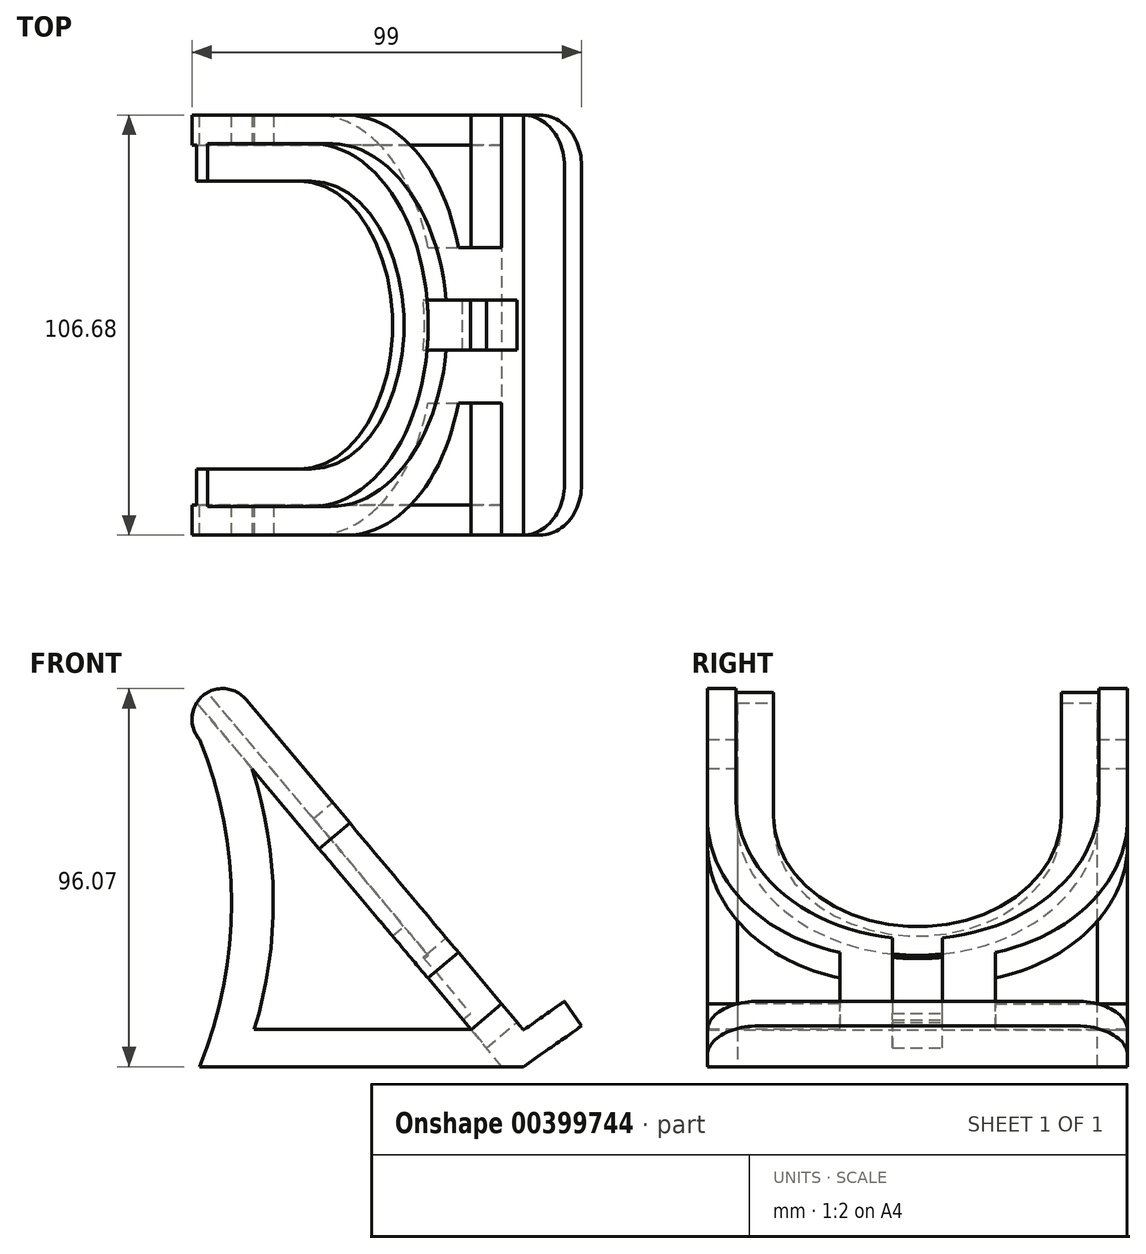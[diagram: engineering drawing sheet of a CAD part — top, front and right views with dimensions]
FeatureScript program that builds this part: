
annotation { "Feature Type Name" : "Feature", "Feature Type Description" : "" }
export const myFeature = defineFeature(function(context is Context, id is Id, definition is map)
    precondition{}
    {
        {
            var Q0;
            Q0=qCreatedBy(makeId("Front.planeOp"),FACE);
            var sketch = newSketch(context, id + "F0", { "sketchPlane" : qUnion([Q0])});
            skLineSegment(sketch, "E0", {"start": v(-26.46, -52) * mm, "end": v(55.88, -52) * mm});
            skLineSegment(sketch, "E1", {"start": v(55.88, -52) * mm, "end": v(70.65, -41.63) * mm});
            skLineSegment(sketch, "E2", {"start": v(70.65, -41.63) * mm, "end": v(66.27, -35.4) * mm});
            skLineSegment(sketch, "E3", {"start": v(66.27, -35.4) * mm, "end": v(55.88, -42.68) * mm});
            skLineSegment(sketch, "E4", {"start": v(55.88, -42.68) * mm, "end": v(-14.6, 41.3) * mm});
            skArc(sketch, "E5", {"start": v(-26.46, -52) * mm, "mid": v(-18.29, -10.4) * mm, "end": v(-26.46, 31.2) * mm});
            skArc(sketch, "E6", {"start": v(-14.6, 41.3) * mm, "mid": v(-25.6, 42.22) * mm, "end": v(-26.46, 31.2) * mm});
            skSolve(sketch);
        }
        {
            var Q0;
            Q0=makeQuery(id+"F0.imprint","IMPRINT",FACE,{"disambiguationData":[TD([[makeQuery(id+"F0.imprint","IMPRINT",EDGE,{"derivedFrom":sQuery(id+"F0.wireOp",EDGE,"E0")}),1.0]])]});
            var Q1;
            Q1 = qSketchRegion(id + "F2", true);
            extrude(context, id + "F1", {"entities" : qUnion([Q0, Q1]), "endBound" : BoundingType.SYMMETRIC, "depth" : 106.68 * mm});
        }
        {
            var Q0;
            Q0=makeQuery(id+"F1.opExtrude","SWEPT_FACE",FACE,{"disambiguationData":[OSD([sQuery(id+"F0.wireOp",EDGE,"E4")])]});
            var sketch = newSketch(context, id + "F2", { "sketchPlane" : qUnion([Q0])});
            skCircle(sketch, "E7", {"center": v(0, 7.58) * mm, "radius": 46.1 * mm});
            skLineSegment(sketch, "E8", {"start": v(0, 7.58) * mm, "end": v(-46.1, 7.58) * mm, "construction": true});
            skLineSegment(sketch, "E9", {"start": v(-46.1, 7.58) * mm, "end": v(-46.1, 73.2) * mm});
            skLineSegment(sketch, "E10", {"start": v(-46.1, 73.2) * mm, "end": v(0, 73.2) * mm});
            skLineSegment(sketch, "E11", {"start": v(0, 73.2) * mm, "end": v(0, 7.58) * mm});
            skLineSegment(sketch, "E12", {"start": v(-46.1, 7.58) * mm, "end": v(0, 7.58) * mm});
            skLineSegment(sketch, "E13.MirrorCS", {"start": v(0, 1.39) * mm, "end": v(46.1, 1.39) * mm, "construction": true});
            skLineSegment(sketch, "E14.MirrorCS", {"start": v(46.1, -1.53) * mm, "end": v(46.05, 73.08) * mm});
            skLineSegment(sketch, "E15.MirrorCS", {"start": v(46.05, 73.08) * mm, "end": v(0, 73.2) * mm});
            skLineSegment(sketch, "E16", {"start": v(-6.35, -38.08) * mm, "end": v(-6.35, -66.02) * mm});
            skLineSegment(sketch, "E17", {"start": v(-6.35, -66.02) * mm, "end": v(6.35, -66.02) * mm});
            skLineSegment(sketch, "E18", {"start": v(6.35, -66.02) * mm, "end": v(6.35, -38.08) * mm});
            skCircle(sketch, "E19", {"center": v(0, 7.58) * mm, "radius": 36.56 * mm});
            skLineSegment(sketch, "E20", {"start": v(-36.56, 7.58) * mm, "end": v(-36.56, 73.2) * mm});
            skLineSegment(sketch, "E21.MirrorCS", {"start": v(36.56, 7.58) * mm, "end": v(36.56, 73.2) * mm});
            skLineSegment(sketch, "E22", {"start": v(-6.35, -56.67) * mm, "end": v(6.35, -56.67) * mm});
            skArc(sketch, "E23", {"start": v(-53.34, 0) * mm, "mid": v(-42.57, -28.16) * mm, "end": v(-16.69, -43.64) * mm});
            skLineSegment(sketch, "E24", {"start": v(-19.75, -42.9) * mm, "end": v(-19.75, -59.96) * mm});
            skLineSegment(sketch, "E25", {"start": v(-19.75, -59.96) * mm, "end": v(-53.34, -59.96) * mm});
            skLineSegment(sketch, "E26", {"start": v(-53.34, -59.96) * mm, "end": v(-53.34, 0) * mm});
            skArc(sketch, "E27.MirrorCS", {"start": v(53.34, 0) * mm, "mid": v(42.57, -28.16) * mm, "end": v(16.69, -43.64) * mm});
            skLineSegment(sketch, "E28.MirrorCS", {"start": v(19.75, -42.9) * mm, "end": v(19.75, -59.96) * mm});
            skLineSegment(sketch, "E29.MirrorCS", {"start": v(19.75, -59.96) * mm, "end": v(53.34, -59.96) * mm});
            skLineSegment(sketch, "E30.MirrorCS", {"start": v(53.34, -59.96) * mm, "end": v(53.34, 0) * mm});
            skSolve(sketch);
        }
        {
            var Q0;
            {var subQ1=sQuery(id+"F2.wireOp",EDGE,"E7");var subQ3=sQuery(id+"F2.wireOp",EDGE,"E20");var subQ4=makeQuery(id+"F2.imprint","INTERSECT",VERTEX,{"derivedFrom":[subQ1,subQ3]});Q0=makeQuery(id+"F2.imprint","IMPRINT",FACE,{"disambiguationData":[TD([[makeQuery(id+"F2.imprint","IMPRINT",EDGE,{"disambiguationData":[TD([[subQ4,-1.0]])],"derivedFrom":subQ1}),1.0]])]});}
            var Q1;
            {var subQ0=sQuery(id+"F2.wireOp",EDGE,"E21.MirrorCS");var subQ1=sQuery(id+"F2.wireOp",EDGE,"E7");var subQ2=makeQuery(id+"F2.imprint","INTERSECT",VERTEX,{"derivedFrom":[subQ1,subQ0]});Q1=makeQuery(id+"F2.imprint","IMPRINT",FACE,{"disambiguationData":[TD([[makeQuery(id+"F2.imprint","IMPRINT",EDGE,{"disambiguationData":[TD([[subQ2,1.0]])],"derivedFrom":subQ1}),-1.0]])]});}
            var Q2;
            {var subQ0=sQuery(id+"F2.wireOp",EDGE,"E11");var subQ3=sQuery(id+"F2.wireOp",EDGE,"E7");var subQ4=makeQuery(id+"F2.imprint","INTERSECT",VERTEX,{"derivedFrom":[subQ3,subQ0]});Q2=makeQuery(id+"F2.imprint","IMPRINT",FACE,{"disambiguationData":[TD([[makeQuery(id+"F2.imprint","IMPRINT",EDGE,{"disambiguationData":[TD([[subQ4,-1.0]])],"derivedFrom":subQ3}),-1.0]])]});}
            var Q3;
            {var subQ0=sQuery(id+"F2.wireOp",EDGE,"E10");var subQ1=sQuery(id+"F2.wireOp",EDGE,"E9");var subQ2=makeQuery(id+"F2.imprint","INTERSECT",VERTEX,{"derivedFrom":[subQ1,subQ0]});Q3=makeQuery(id+"F2.imprint","IMPRINT",FACE,{"disambiguationData":[TD([[makeQuery(id+"F2.imprint","IMPRINT",EDGE,{"disambiguationData":[TD([[subQ2,-1.0]])],"derivedFrom":subQ0}),-1.0]])]});}
            var Q4;
            {var subQ0=sQuery(id+"F2.wireOp",EDGE,"E15.MirrorCS");var subQ1=sQuery(id+"F2.wireOp",EDGE,"E14.MirrorCS");var subQ2=makeQuery(id+"F2.imprint","INTERSECT",VERTEX,{"derivedFrom":[subQ1,subQ0]});Q4=makeQuery(id+"F2.imprint","IMPRINT",FACE,{"disambiguationData":[TD([[makeQuery(id+"F2.imprint","IMPRINT",EDGE,{"disambiguationData":[TD([[subQ2,-1.0]])],"derivedFrom":subQ0}),1.0]])]});}
            var Q5;
            {var subQ0=sQuery(id+"F2.wireOp",EDGE,"E11");var subQ1=sQuery(id+"F2.wireOp",EDGE,"E7");var subQ2=makeQuery(id+"F2.imprint","INTERSECT",VERTEX,{"derivedFrom":[subQ1,subQ0]});Q5=makeQuery(id+"F2.imprint","IMPRINT",FACE,{"disambiguationData":[TD([[makeQuery(id+"F2.imprint","IMPRINT",EDGE,{"disambiguationData":[TD([[subQ2,-1.0]])],"derivedFrom":subQ1}),1.0]])]});}
            var Q6;
            {var subQ0=sQuery(id+"F2.wireOp",EDGE,"E11");var subQ1=sQuery(id+"F2.wireOp",EDGE,"E7");var subQ2=makeQuery(id+"F2.imprint","INTERSECT",VERTEX,{"derivedFrom":[subQ1,subQ0]});Q6=makeQuery(id+"F2.imprint","IMPRINT",FACE,{"disambiguationData":[TD([[makeQuery(id+"F2.imprint","IMPRINT",EDGE,{"disambiguationData":[TD([[subQ2,1.0]])],"derivedFrom":subQ1}),1.0]])]});}
            var Q7;
            {var subQ1=sQuery(id+"F2.wireOp",EDGE,"E7");var subQ3=sQuery(id+"F2.wireOp",EDGE,"E20");var subQ4=makeQuery(id+"F2.imprint","INTERSECT",VERTEX,{"derivedFrom":[subQ1,subQ3]});Q7=makeQuery(id+"F2.imprint","IMPRINT",FACE,{"disambiguationData":[TD([[makeQuery(id+"F2.imprint","IMPRINT",EDGE,{"disambiguationData":[TD([[subQ4,-1.0]])],"derivedFrom":subQ1}),-1.0]])]});}
            var Q8;
            {var subQ5=sQuery(id+"F2.wireOp",EDGE,"E11");var subQ7=sQuery(id+"F2.wireOp",EDGE,"E7");var subQ8=makeQuery(id+"F2.imprint","INTERSECT",VERTEX,{"derivedFrom":[subQ7,subQ5]});Q8=makeQuery(id+"F2.imprint","IMPRINT",FACE,{"disambiguationData":[TD([[makeQuery(id+"F2.imprint","IMPRINT",EDGE,{"disambiguationData":[TD([[subQ8,1.0]])],"derivedFrom":subQ7}),-1.0]])]});}
            var Q9;
            {var subQ0=sQuery(id+"F2.wireOp",EDGE,"E20");var subQ1=sQuery(id+"F2.wireOp",EDGE,"E7");var subQ2=makeQuery(id+"F2.imprint","INTERSECT",VERTEX,{"derivedFrom":[subQ1,subQ0]});Q9=makeQuery(id+"F2.imprint","IMPRINT",FACE,{"disambiguationData":[TD([[makeQuery(id+"F2.imprint","IMPRINT",EDGE,{"disambiguationData":[TD([[subQ2,1.0]])],"derivedFrom":subQ1}),-1.0]])]});}
            var Q10;
            {var subQ0=sQuery(id+"F2.wireOp",EDGE,"E20");var subQ3=sQuery(id+"F2.wireOp",EDGE,"E7");var subQ4=makeQuery(id+"F2.imprint","INTERSECT",VERTEX,{"derivedFrom":[subQ3,subQ0]});Q10=makeQuery(id+"F2.imprint","IMPRINT",FACE,{"disambiguationData":[TD([[makeQuery(id+"F2.imprint","IMPRINT",EDGE,{"disambiguationData":[TD([[subQ4,1.0]])],"derivedFrom":subQ3}),1.0]])]});}
            var Q11;
            {var subQ0=sQuery(id+"F2.wireOp",EDGE,"E21.MirrorCS");var subQ1=sQuery(id+"F2.wireOp",EDGE,"E19");var subQ2=makeQuery(id+"F2.imprint","INTERSECT",VERTEX,{"derivedFrom":[subQ1,subQ0]});Q11=makeQuery(id+"F2.imprint","IMPRINT",FACE,{"disambiguationData":[TD([[makeQuery(id+"F2.imprint","IMPRINT",EDGE,{"disambiguationData":[TD([[subQ2,-1.0]])],"derivedFrom":subQ1}),-1.0]])]});}
            var Q12;
            {var subQ0=sQuery(id+"F2.wireOp",EDGE,"E7");var subQ7=sQuery(id+"F2.wireOp",EDGE,"E21.MirrorCS");var subQ11=makeQuery(id+"F2.imprint","INTERSECT",VERTEX,{"derivedFrom":[subQ0,subQ7]});Q12=makeQuery(id+"F2.imprint","IMPRINT",FACE,{"disambiguationData":[TD([[makeQuery(id+"F2.imprint","IMPRINT",EDGE,{"disambiguationData":[TD([[subQ11,1.0]])],"derivedFrom":subQ0}),1.0]])]});}
            var Q13;
            {var subQ0=sQuery(id+"F2.wireOp",EDGE,"E12");var subQ1=sQuery(id+"F2.wireOp",EDGE,"E11");var subQ2=makeQuery(id+"F2.imprint","INTERSECT",VERTEX,{"derivedFrom":[subQ1,subQ0]});Q13=makeQuery(id+"F2.imprint","IMPRINT",FACE,{"disambiguationData":[TD([[makeQuery(id+"F2.imprint","IMPRINT",EDGE,{"disambiguationData":[TD([[subQ2,1.0]])],"derivedFrom":subQ1}),1.0]])]});}
            var Q14;
            {var subQ0=sQuery(id+"F2.wireOp",EDGE,"E12");var subQ1=sQuery(id+"F2.wireOp",EDGE,"E11");var subQ2=makeQuery(id+"F2.imprint","INTERSECT",VERTEX,{"derivedFrom":[subQ1,subQ0]});Q14=makeQuery(id+"F2.imprint","IMPRINT",FACE,{"disambiguationData":[TD([[makeQuery(id+"F2.imprint","IMPRINT",EDGE,{"disambiguationData":[TD([[subQ2,1.0]])],"derivedFrom":subQ1}),-1.0]])]});}
            var Q15;
            {var subQ0=sQuery(id+"F2.wireOp",EDGE,"E21.MirrorCS");var subQ1=sQuery(id+"F2.wireOp",EDGE,"E7");var subQ2=makeQuery(id+"F2.imprint","INTERSECT",VERTEX,{"derivedFrom":[subQ1,subQ0]});Q15=makeQuery(id+"F2.imprint","IMPRINT",FACE,{"disambiguationData":[TD([[makeQuery(id+"F2.imprint","IMPRINT",EDGE,{"disambiguationData":[TD([[subQ2,-1.0]])],"derivedFrom":subQ1}),-1.0]])]});}
            extrude(context, id + "F3", {"entities" : qUnion([Q0, Q1, Q2, Q3, Q4, Q5, Q6, Q7, Q8, Q9, Q10, Q11, Q12, Q13, Q14, Q15]), "operationType" : NewBodyOperationType.REMOVE, "oppositeDirection" : true, "depth" : 6.35 * mm});
        }
        {
            var Q0;
            {var subQ0=sQuery(id+"F2.wireOp",EDGE,"E16");Q0=makeQuery(id+"F2.imprint","IMPRINT",FACE,{"disambiguationData":[TD([[makeQuery(id+"F2.imprint","IMPRINT",EDGE,{"derivedFrom":subQ0}),1.0]])]});}
            extrude(context, id + "F4", {"entities" : qUnion([Q0]), "operationType" : NewBodyOperationType.REMOVE, "oppositeDirection" : true, "depth" : 7.62 * mm});
        }
        {
            var Q0;
            Q0=makeQuery(id+"F1.opExtrude","CAP_FACE",FACE,{"disambiguationData":[OSD([sQuery(id+"F0.wireOp",EDGE,"E0"),sQuery(id+"F0.wireOp",EDGE,"E1"),sQuery(id+"F0.wireOp",EDGE,"E2"),sQuery(id+"F0.wireOp",EDGE,"E3"),sQuery(id+"F0.wireOp",EDGE,"E4"),sQuery(id+"F0.wireOp",EDGE,"E5"),sQuery(id+"F0.wireOp",EDGE,"E6")])],"isStart":false});
            var sketch = newSketch(context, id + "F5", { "sketchPlane" : qUnion([Q0])});
            skLineSegment(sketch, "E31", {"start": v(-13.05, 23.66) * mm, "end": v(42.5, -42.55) * mm});
            skArc(sketch, "E32", {"start": v(-12.51, -42.55) * mm, "mid": v(-7.68, -9.4) * mm, "end": v(-13.05, 23.66) * mm});
            skLineSegment(sketch, "E33", {"start": v(-12.51, -42.55) * mm, "end": v(42.5, -42.55) * mm});
            skSolve(sketch);
        }
        {
            var Q0;
            Q0=makeQuery(id+"F5.imprint","IMPRINT",FACE,{"disambiguationData":[TD([[makeQuery(id+"F5.imprint","IMPRINT",EDGE,{"derivedFrom":sQuery(id+"F5.wireOp",EDGE,"E31")}),-1.0]])]});
            var Q1;
            Q1=makeQuery(id+"F5.imprint","IMPRINT",FACE,{"disambiguationData":[TD([[makeQuery(id+"F5.imprint","IMPRINT",EDGE,{"derivedFrom":sQuery(id+"F5.wireOp",EDGE,"wPjwQzWi-Tjyw-v6FZ-FHt0-rqqnCeeGMehr")}),-1.0]])]});
            extrude(context, id + "F6", {"entities" : qUnion([Q0, Q1]), "operationType" : NewBodyOperationType.REMOVE, "endBound" : BoundingType.UP_TO_NEXT, "oppositeDirection" : true, "depth" : 25.4 * mm});
        }
        {
            var Q0;
            Q0=makeQuery(id+"F1.opExtrude","SWEPT_EDGE",EDGE,{"disambiguationData":[OSD([sQuery(id+"F0.wireOp",EDGE,"E0"),sQuery(id+"F0.wireOp",EDGE,"E5")])]});
            cPlane(context, id + "F7", {"entities" : qUnion([Q0]), "cplaneType" : CPlaneType.LINE_ANGLE, "offset" : 40.4 * mm, "angle" : 50 * degree, "width" : 152.4 * mm, "height" : 152.4 * mm});
        }
        {
            var Q0;
            Q0=qCreatedBy(id+"F7.planeOp",FACE);
            var sketch = newSketch(context, id + "F8", { "sketchPlane" : qUnion([Q0])});
            skLineSegment(sketch, "E34", {"start": v(45.72, 83.56) * mm, "end": v(-45.72, 83.56) * mm});
            skLineSegment(sketch, "E35", {"start": v(-45.72, 83.56) * mm, "end": v(-45.72, -100.06) * mm});
            skLineSegment(sketch, "E36", {"start": v(-45.72, -100.06) * mm, "end": v(45.72, -100.06) * mm});
            skLineSegment(sketch, "E37", {"start": v(45.72, -100.06) * mm, "end": v(45.72, 83.56) * mm});
            skSolve(sketch);
        }
        {
            var Q0;
            Q0=makeQuery(id+"F8.imprint","IMPRINT",FACE,{"disambiguationData":[TD([[makeQuery(id+"F8.imprint","IMPRINT",EDGE,{"derivedFrom":sQuery(id+"F8.wireOp",EDGE,"E34")}),1.0]])]});
            extrude(context, id + "F9", {"entities" : qUnion([Q0]), "operationType" : NewBodyOperationType.REMOVE, "depth" : 58.93 * mm});
        }
        {
            var Q0;
            {var subQ0=sQuery(id+"F2.wireOp",EDGE,"E12");var subQ1=sQuery(id+"F2.wireOp",EDGE,"E11");var subQ2=makeQuery(id+"F2.imprint","INTERSECT",VERTEX,{"derivedFrom":[subQ1,subQ0]});Q0=makeQuery(id+"F2.imprint","IMPRINT",FACE,{"disambiguationData":[TD([[makeQuery(id+"F2.imprint","IMPRINT",EDGE,{"disambiguationData":[TD([[subQ2,1.0]])],"derivedFrom":subQ1}),-1.0]])]});}
            var Q1;
            {var subQ0=sQuery(id+"F2.wireOp",EDGE,"E12");var subQ1=sQuery(id+"F2.wireOp",EDGE,"E11");var subQ2=makeQuery(id+"F2.imprint","INTERSECT",VERTEX,{"derivedFrom":[subQ1,subQ0]});Q1=makeQuery(id+"F2.imprint","IMPRINT",FACE,{"disambiguationData":[TD([[makeQuery(id+"F2.imprint","IMPRINT",EDGE,{"disambiguationData":[TD([[subQ2,1.0]])],"derivedFrom":subQ1}),1.0]])]});}
            var Q2;
            {var subQ0=sQuery(id+"F2.wireOp",EDGE,"E20");var subQ3=sQuery(id+"F2.wireOp",EDGE,"E7");var subQ4=makeQuery(id+"F2.imprint","INTERSECT",VERTEX,{"derivedFrom":[subQ3,subQ0]});Q2=makeQuery(id+"F2.imprint","IMPRINT",FACE,{"disambiguationData":[TD([[makeQuery(id+"F2.imprint","IMPRINT",EDGE,{"disambiguationData":[TD([[subQ4,1.0]])],"derivedFrom":subQ3}),1.0]])]});}
            var Q3;
            {var subQ0=sQuery(id+"F2.wireOp",EDGE,"E21.MirrorCS");var subQ1=sQuery(id+"F2.wireOp",EDGE,"E19");var subQ2=makeQuery(id+"F2.imprint","INTERSECT",VERTEX,{"derivedFrom":[subQ1,subQ0]});Q3=makeQuery(id+"F2.imprint","IMPRINT",FACE,{"disambiguationData":[TD([[makeQuery(id+"F2.imprint","IMPRINT",EDGE,{"disambiguationData":[TD([[subQ2,-1.0]])],"derivedFrom":subQ1}),-1.0]])]});}
            var Q4;
            {var subQ0=sQuery(id+"F2.wireOp",EDGE,"E11");var subQ1=sQuery(id+"F2.wireOp",EDGE,"E7");var subQ2=makeQuery(id+"F2.imprint","INTERSECT",VERTEX,{"derivedFrom":[subQ1,subQ0]});Q4=makeQuery(id+"F2.imprint","IMPRINT",FACE,{"disambiguationData":[TD([[makeQuery(id+"F2.imprint","IMPRINT",EDGE,{"disambiguationData":[TD([[subQ2,1.0]])],"derivedFrom":subQ1}),1.0]])]});}
            var Q5;
            {var subQ0=sQuery(id+"F2.wireOp",EDGE,"E11");var subQ1=sQuery(id+"F2.wireOp",EDGE,"E7");var subQ2=makeQuery(id+"F2.imprint","INTERSECT",VERTEX,{"derivedFrom":[subQ1,subQ0]});Q5=makeQuery(id+"F2.imprint","IMPRINT",FACE,{"disambiguationData":[TD([[makeQuery(id+"F2.imprint","IMPRINT",EDGE,{"disambiguationData":[TD([[subQ2,-1.0]])],"derivedFrom":subQ1}),1.0]])]});}
            var Q6;
            {var subQ0=sQuery(id+"F2.wireOp",EDGE,"E11");var subQ3=sQuery(id+"F2.wireOp",EDGE,"E7");var subQ4=makeQuery(id+"F2.imprint","INTERSECT",VERTEX,{"derivedFrom":[subQ3,subQ0]});Q6=makeQuery(id+"F2.imprint","IMPRINT",FACE,{"disambiguationData":[TD([[makeQuery(id+"F2.imprint","IMPRINT",EDGE,{"disambiguationData":[TD([[subQ4,-1.0]])],"derivedFrom":subQ3}),-1.0]])]});}
            var Q7;
            {var subQ0=sQuery(id+"F2.wireOp",EDGE,"E20");var subQ1=sQuery(id+"F2.wireOp",EDGE,"E7");var subQ2=makeQuery(id+"F2.imprint","INTERSECT",VERTEX,{"derivedFrom":[subQ1,subQ0]});Q7=makeQuery(id+"F2.imprint","IMPRINT",FACE,{"disambiguationData":[TD([[makeQuery(id+"F2.imprint","IMPRINT",EDGE,{"disambiguationData":[TD([[subQ2,1.0]])],"derivedFrom":subQ1}),-1.0]])]});}
            var Q8;
            {var subQ5=sQuery(id+"F2.wireOp",EDGE,"E11");var subQ7=sQuery(id+"F2.wireOp",EDGE,"E7");var subQ8=makeQuery(id+"F2.imprint","INTERSECT",VERTEX,{"derivedFrom":[subQ7,subQ5]});Q8=makeQuery(id+"F2.imprint","IMPRINT",FACE,{"disambiguationData":[TD([[makeQuery(id+"F2.imprint","IMPRINT",EDGE,{"disambiguationData":[TD([[subQ8,1.0]])],"derivedFrom":subQ7}),-1.0]])]});}
            var Q9;
            {var subQ0=sQuery(id+"F2.wireOp",EDGE,"E21.MirrorCS");var subQ1=sQuery(id+"F2.wireOp",EDGE,"E7");var subQ2=makeQuery(id+"F2.imprint","INTERSECT",VERTEX,{"derivedFrom":[subQ1,subQ0]});Q9=makeQuery(id+"F2.imprint","IMPRINT",FACE,{"disambiguationData":[TD([[makeQuery(id+"F2.imprint","IMPRINT",EDGE,{"disambiguationData":[TD([[subQ2,-1.0]])],"derivedFrom":subQ1}),-1.0]])]});}
            var Q10;
            {var subQ0=sQuery(id+"F2.wireOp",EDGE,"E19");var subQ1=sQuery(id+"F2.wireOp",EDGE,"E11");var subQ2=makeQuery(id+"F2.imprint","INTERSECT",VERTEX,{"derivedFrom":[subQ1,subQ0]});Q10=makeQuery(id+"F2.imprint","IMPRINT",FACE,{"disambiguationData":[TD([[makeQuery(id+"F2.imprint","IMPRINT",EDGE,{"disambiguationData":[TD([[subQ2,-1.0]])],"derivedFrom":subQ1}),1.0]])]});}
            var Q11;
            {var subQ0=sQuery(id+"F2.wireOp",EDGE,"E19");var subQ1=sQuery(id+"F2.wireOp",EDGE,"E11");var subQ2=makeQuery(id+"F2.imprint","INTERSECT",VERTEX,{"derivedFrom":[subQ1,subQ0]});Q11=makeQuery(id+"F2.imprint","IMPRINT",FACE,{"disambiguationData":[TD([[makeQuery(id+"F2.imprint","IMPRINT",EDGE,{"disambiguationData":[TD([[subQ2,-1.0]])],"derivedFrom":subQ1}),-1.0]])]});}
            extrude(context, id + "F10", {"entities" : qUnion([Q0, Q1, Q2, Q3, Q4, Q5, Q6, Q7, Q8, Q9, Q10, Q11]), "operationType" : NewBodyOperationType.REMOVE, "oppositeDirection" : true, "depth" : 25.4 * mm});
        }
        {
            var Q0;
            {var subQ0=sQuery(id+"F2.wireOp",EDGE,"E17");Q0=makeQuery(id+"F2.imprint","IMPRINT",FACE,{"disambiguationData":[TD([[makeQuery(id+"F2.imprint","IMPRINT",EDGE,{"derivedFrom":subQ0}),1.0]])]});}
            extrude(context, id + "F11", {"entities" : qUnion([Q0]), "operationType" : NewBodyOperationType.REMOVE, "endBound" : BoundingType.THROUGH_ALL, "oppositeDirection" : true, "depth" : 25.4 * mm});
        }
        {
            var Q0;
            Q0=makeQuery(id+"F1.opExtrude","CAP_EDGE",EDGE,{"disambiguationData":[OSD([sQuery(id+"F0.wireOp",EDGE,"E2")])],"isStart":false});
            var Q1;
            Q1=makeQuery(id+"F1.opExtrude","CAP_EDGE",EDGE,{"disambiguationData":[OSD([sQuery(id+"F0.wireOp",EDGE,"E2")])],"isStart":true});
            fillet(context, id + "F12", {"entities" : qUnion([Q0, Q1]), "radius" : 12.88 * mm, "tangentPropagation" : true, "allowEdgeOverflow" : false});
        }
        {
            var Q0;
            {var subQ2=sQuery(id+"F2.wireOp",EDGE,"E24");Q0=makeQuery(id+"F2.imprint","IMPRINT",FACE,{"disambiguationData":[TD([[makeQuery(id+"F2.imprint","IMPRINT",EDGE,{"derivedFrom":subQ2}),-1.0]])]});}
            var Q1;
            {var subQ2=sQuery(id+"F2.wireOp",EDGE,"E28.MirrorCS");Q1=makeQuery(id+"F2.imprint","IMPRINT",FACE,{"disambiguationData":[TD([[makeQuery(id+"F2.imprint","IMPRINT",EDGE,{"derivedFrom":subQ2}),1.0]])]});}
            extrude(context, id + "F13", {"entities" : qUnion([Q0, Q1]), "operationType" : NewBodyOperationType.REMOVE, "oppositeDirection" : true, "depth" : 10.16 * mm});
        }
    });
